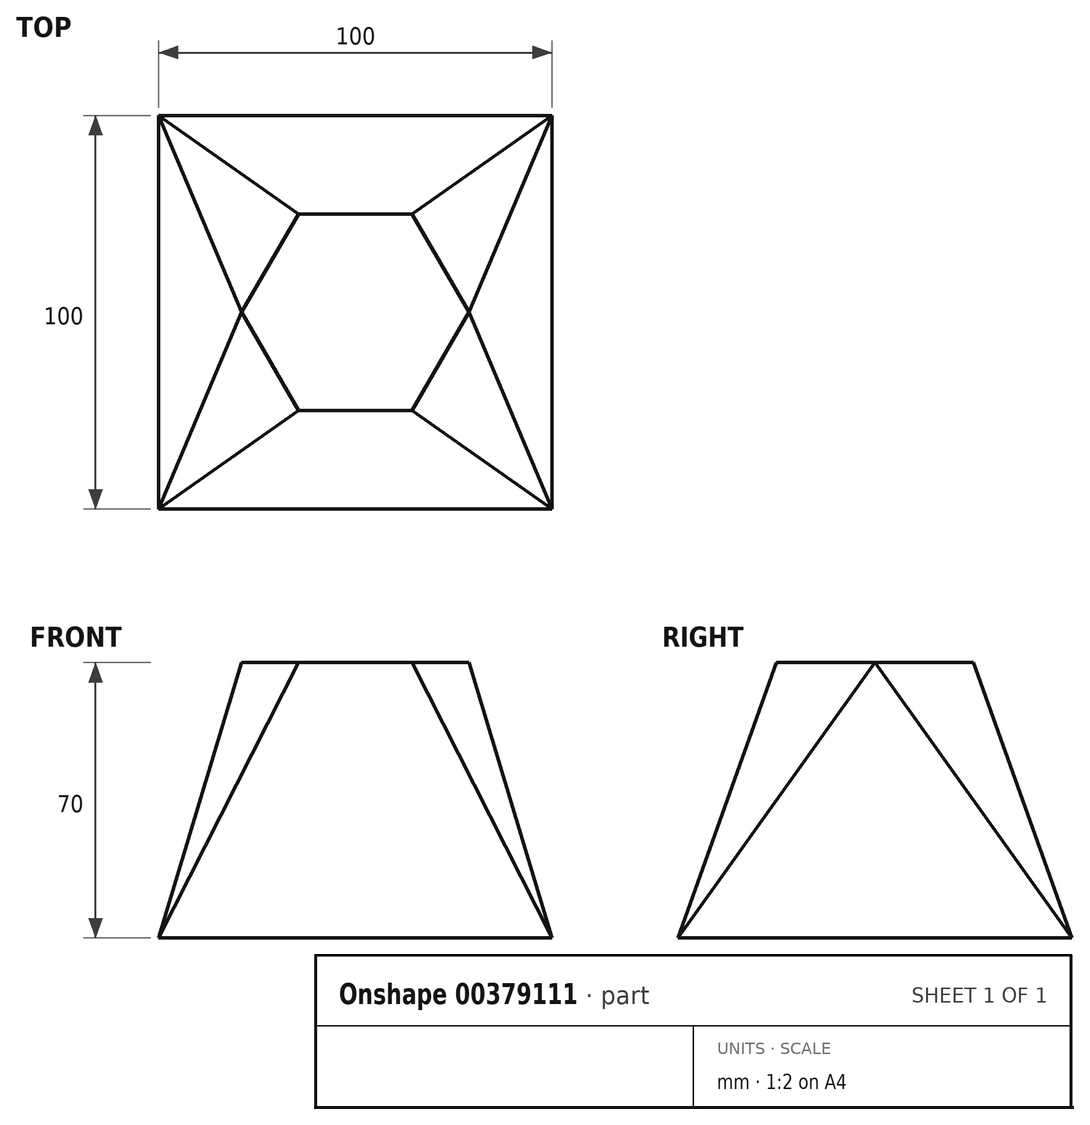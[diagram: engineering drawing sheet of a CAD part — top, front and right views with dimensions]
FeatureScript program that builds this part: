
annotation { "Feature Type Name" : "Feature", "Feature Type Description" : "" }
export const myFeature = defineFeature(function(context is Context, id is Id, definition is map)
    precondition{}
    {
        {
            var Q0;
            Q0=qCreatedBy(makeId("Top.planeOp"),FACE);
            var sketch = newSketch(context, id + "F0", { "sketchPlane" : qUnion([Q0])});
            skLineSegment(sketch, "E0.bottom", {"start": v(50, 50) * mm, "end": v(-50, 50) * mm});
            skLineSegment(sketch, "E0.top", {"start": v(50, -50) * mm, "end": v(-50, -50) * mm});
            skLineSegment(sketch, "E0.left", {"start": v(50, 50) * mm, "end": v(50, -50) * mm});
            skLineSegment(sketch, "E0.right", {"start": v(-50, 50) * mm, "end": v(-50, -50) * mm});
            skPoint(sketch, "E0.middle", {"position": v(0, 0) * mm});
            skSolve(sketch);
        }
        {
            var Q0;
            Q0=qCreatedBy(makeId("Top.planeOp"),FACE);
            cPlane(context, id + "F1", {"entities" : qUnion([Q0]), "cplaneType" : CPlaneType.OFFSET, "offset" : 70 * mm, "width" : 150 * mm, "height" : 150 * mm});
        }
        {
            var Q0;
            Q0=qCreatedBy(id+"F1.planeOp",FACE);
            var sketch = newSketch(context, id + "F2", { "sketchPlane" : qUnion([Q0])});
            skCircle(sketch, "E1.cCircle", {"center": v(0, 0) * mm, "radius": 25 * mm, "construction": true});
            skLineSegment(sketch, "E1.0", {"start": v(-14.43, 25) * mm, "end": v(14.43, 25) * mm});
            skLineSegment(sketch, "E1.1", {"start": v(14.43, 25) * mm, "end": v(28.87, 0) * mm});
            skLineSegment(sketch, "E1.2", {"start": v(28.87, 0) * mm, "end": v(14.43, -25) * mm});
            skLineSegment(sketch, "E1.3", {"start": v(14.43, -25) * mm, "end": v(-14.43, -25) * mm});
            skLineSegment(sketch, "E1.4", {"start": v(-14.43, -25) * mm, "end": v(-28.87, 0) * mm});
            skLineSegment(sketch, "E1.5", {"start": v(-28.87, 0) * mm, "end": v(-14.43, 25) * mm});
            skPoint(sketch, "E1.0.midPoint", {"position": v(0, 25) * mm});
            skLineSegment(sketch, "E2.bottom", {"start": v(28.87, 25) * mm, "end": v(-28.87, 25) * mm});
            skLineSegment(sketch, "E2.top", {"start": v(28.87, -25) * mm, "end": v(-28.87, -25) * mm});
            skLineSegment(sketch, "E2.left", {"start": v(28.87, 25) * mm, "end": v(28.87, -25) * mm});
            skLineSegment(sketch, "E2.right", {"start": v(-28.87, 25) * mm, "end": v(-28.87, -25) * mm});
            skSolve(sketch);
        }
        {
            var Q0;
            Q0=qCreatedBy(id+"F1.planeOp",FACE);
            var sketch = newSketch(context, id + "F3", { "sketchPlane" : qUnion([Q0])});
            skLineSegment(sketch, "E3.bottom", {"start": v(28.87, 25) * mm, "end": v(-28.87, 25) * mm});
            skLineSegment(sketch, "E3.top", {"start": v(28.87, -25) * mm, "end": v(-28.87, -25) * mm});
            skLineSegment(sketch, "E3.left", {"start": v(28.87, 25) * mm, "end": v(28.87, -25) * mm});
            skLineSegment(sketch, "E3.right", {"start": v(-28.87, 25) * mm, "end": v(-28.87, -25) * mm});
            skPoint(sketch, "E3.middle", {"position": v(0, 0) * mm});
            skSolve(sketch);
        }
        {
            var Q0;
            Q0=makeQuery(id+"F0.imprint","IMPRINT",FACE,{"disambiguationData":[TD([[makeQuery(id+"F0.imprint","IMPRINT",EDGE,{"derivedFrom":sQuery(id+"F0.wireOp",EDGE,"E0.bottom")}),1.0]])]});
            var Q1;
            Q1 = qSketchRegion(id + "F3", true);
            loft(context, id + "F4", {"sheetProfilesArray" : [{ "sheetProfileEntities" : qUnion([Q0]) }, { "sheetProfileEntities" : qUnion([Q1]) }]});
        }
        {
            var Q1;
            Q1=makeQuery(id+"F4.opLoft","MID_CAP_VERTEX",VERTEX,{"disambiguationData":[OSD([sQuery(id+"F0.wireOp",EDGE,"E0.top"),sQuery(id+"F0.wireOp",EDGE,"E0.right")])],"capPos":0.0});
            var Q2;
            {var subQ0=sQuery(id+"F2.wireOp",EDGE,"E1.4");Q2=makeQuery(id+"F2.imprint","IMPRINT",FACE,{"disambiguationData":[TD([[makeQuery(id+"F2.imprint","IMPRINT",EDGE,{"derivedFrom":subQ0}),1.0]])]});}
            loft(context, id + "F5", {"operationType" : NewBodyOperationType.REMOVE, "sheetProfilesArray" : [{ "sheetProfileEntities" : qUnion([Q1]) }, { "sheetProfileEntities" : qUnion([Q2]) }]});
        }
        {
            var Q1;
            {var subQ0=sQuery(id+"F2.wireOp",EDGE,"E1.2");Q1=makeQuery(id+"F2.imprint","IMPRINT",FACE,{"disambiguationData":[TD([[makeQuery(id+"F2.imprint","IMPRINT",EDGE,{"derivedFrom":subQ0}),1.0]])]});}
            var Q2;
            Q2=sQuery(id+"F0.wireOp",VERTEX,"E0.left.end");
            loft(context, id + "F6", {"operationType" : NewBodyOperationType.REMOVE, "sheetProfilesArray" : [{ "sheetProfileEntities" : qUnion([Q1]) }, { "sheetProfileEntities" : qUnion([Q2]) }]});
        }
        {
            var Q1;
            {var subQ0=sQuery(id+"F2.wireOp",EDGE,"E1.1");Q1=makeQuery(id+"F2.imprint","IMPRINT",FACE,{"disambiguationData":[TD([[makeQuery(id+"F2.imprint","IMPRINT",EDGE,{"derivedFrom":subQ0}),1.0]])]});}
            var Q2;
            Q2=sQuery(id+"F0.wireOp",VERTEX,"E0.left.start");
            loft(context, id + "F7", {"operationType" : NewBodyOperationType.REMOVE, "sheetProfilesArray" : [{ "sheetProfileEntities" : qUnion([Q1]) }, { "sheetProfileEntities" : qUnion([Q2]) }]});
        }
        {
            var Q1;
            {var subQ0=sQuery(id+"F2.wireOp",EDGE,"E1.5");Q1=makeQuery(id+"F2.imprint","IMPRINT",FACE,{"disambiguationData":[TD([[makeQuery(id+"F2.imprint","IMPRINT",EDGE,{"derivedFrom":subQ0}),1.0]])]});}
            var Q2;
            Q2=sQuery(id+"F0.wireOp",VERTEX,"E0.right.start");
            loft(context, id + "F8", {"operationType" : NewBodyOperationType.REMOVE, "sheetProfilesArray" : [{ "sheetProfileEntities" : qUnion([Q1]) }, { "sheetProfileEntities" : qUnion([Q2]) }]});
        }
    });
